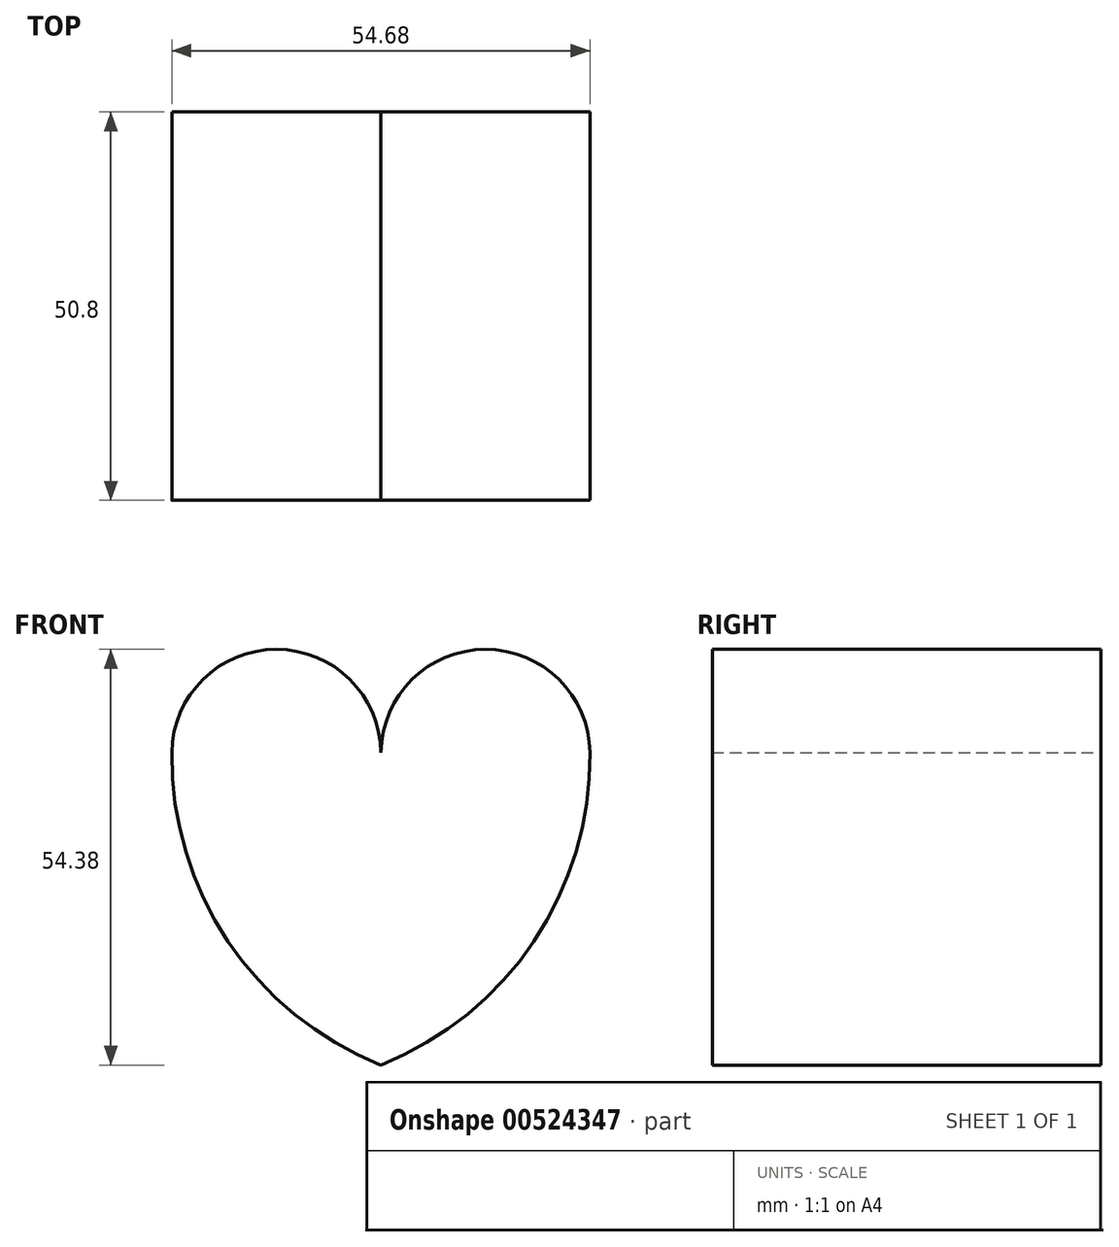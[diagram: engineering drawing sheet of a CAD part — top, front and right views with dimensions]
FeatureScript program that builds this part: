
annotation { "Feature Type Name" : "Feature", "Feature Type Description" : "" }
export const myFeature = defineFeature(function(context is Context, id is Id, definition is map)
    precondition{}
    {
        {
            var Q0;
            Q0=qCreatedBy(makeId("Front.planeOp"),FACE);
            var sketch = newSketch(context, id + "F0", { "sketchPlane" : qUnion([Q0])});
            skArc(sketch, "E0", {"start": v(-27.34, 0) * mm, "mid": v(-20.01, -24.68) * mm, "end": v(0, -40.87) * mm});
            skArc(sketch, "E1", {"start": v(-27.34, 0) * mm, "mid": v(-13.67, 13.5) * mm, "end": v(0, 0) * mm});
            skArc(sketch, "E2.MirrorCS", {"start": v(27.34, 0) * mm, "mid": v(13.67, 13.5) * mm, "end": v(0, 0) * mm});
            skArc(sketch, "E3.MirrorCS", {"start": v(27.34, 0) * mm, "mid": v(20.01, -24.68) * mm, "end": v(0, -40.87) * mm});
            skSolve(sketch);
        }
        {
            var Q0;
            Q0=makeQuery(id+"F0.imprint","IMPRINT",FACE,{"disambiguationData":[TD([[makeQuery(id+"F0.imprint","IMPRINT",EDGE,{"derivedFrom":sQuery(id+"F0.wireOp",EDGE,"E0")}),1.0]])]});
            extrude(context, id + "F1", {"entities" : qUnion([Q0]), "depth" : 25.4 * mm, "offsetDistance" : 25.4 * mm, "hasSecondDirection" : true, "secondDirectionOppositeDirection" : true, "secondDirectionDepth" : 25.4 * mm});
        }
    });
